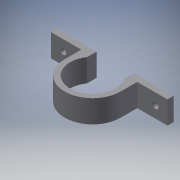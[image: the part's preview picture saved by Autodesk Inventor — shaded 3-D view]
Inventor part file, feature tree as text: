
AUTODESK INVENTOR PART (.ipt)
format: ipt  version: 2016 (Build 200138000, 138)  size: 119,808 bytes
history: native  units: in
note: dims shown in document units (in); Inventor stores cm internally (conversion verified against a paired STEP export)
features: hole x2, extrude x1, sketch x1
ambient origin geometry x8: Origin, YZ Plane, XZ Plane, XY Plane, X Axis, Y Axis, Z Axis, Center Point
bodies: Solid1 (feature_tree)
feature tree (4):
  extrude  "Extrusion1"  Depth=1.4567in
  hole  "Hole1"  [1 undecoded]
  hole  "Hole2"  [1 undecoded]
  sketch  "Sketch1"  dims[d0=1.1811in d1=1.4567in d2=0.1575in d3=0.1575in d4=0.7874in d5=0.7874in d10=0.5906in d11=0.0in d12=0.2756in d13=0.315in d14=0.1575in d15=0.2362in d16=0.1575in d17=0.0787in d18=90.0deg d19=0.315in d20=0.8108in d21=0.2953in d22=0.315in d23=0.1575in d24=0.2362in d25=0.1575in d26=0.0787in d27=90.0deg d28=0.315in d29=0.8108in d30=0.0394in d31=0.0394in]
note: 2 required parameter values undecoded (feature->parameter linkage not recoverable at this tier; creation-order binding heuristic only, values carry confidence <= 0.55)
